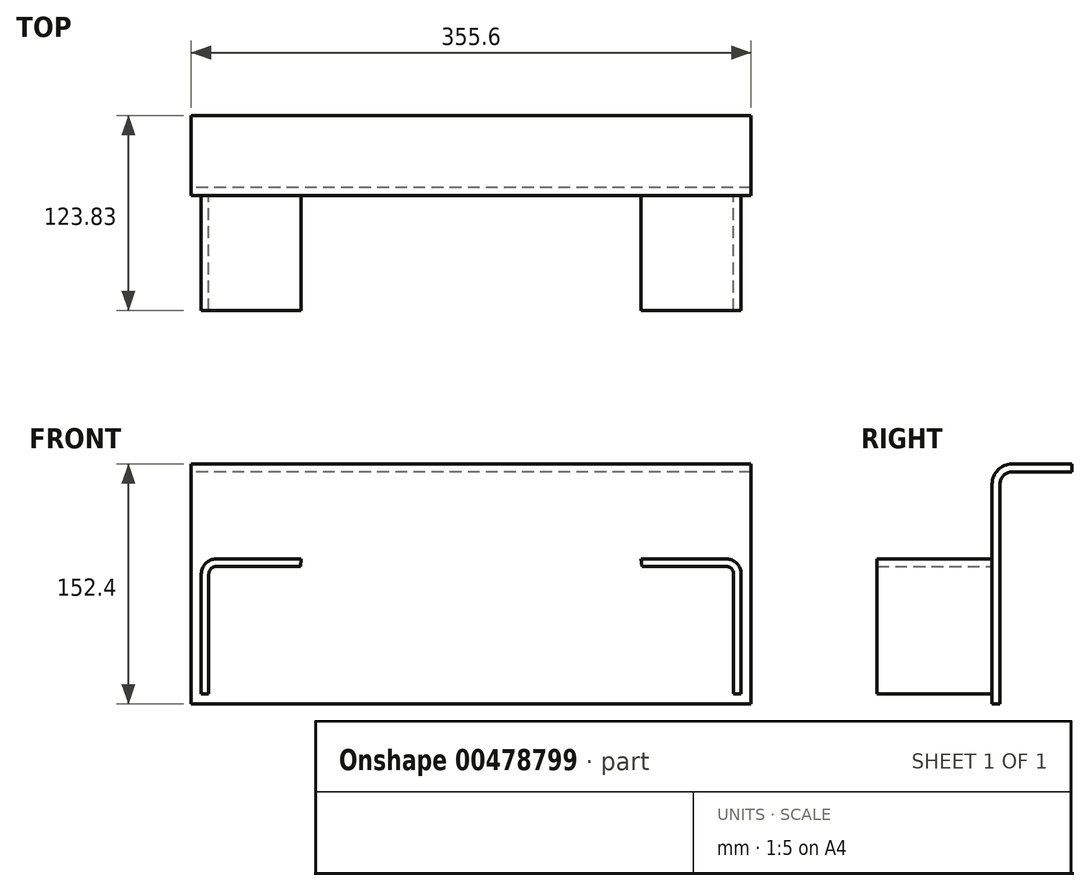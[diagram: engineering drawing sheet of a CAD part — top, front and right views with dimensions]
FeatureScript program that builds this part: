
annotation { "Feature Type Name" : "Feature", "Feature Type Description" : "" }
export const myFeature = defineFeature(function(context is Context, id is Id, definition is map)
    precondition{}
    {
        {
            var Q0;
            Q0=qCreatedBy(makeId("Right.planeOp"),FACE);
            var sketch = newSketch(context, id + "F0", { "sketchPlane" : qUnion([Q0])});
            skLineSegment(sketch, "E0", {"start": v(0, -152.4) * mm, "end": v(0, -12.7) * mm});
            skLineSegment(sketch, "E1", {"start": v(12.7, 0) * mm, "end": v(50.8, 0) * mm});
            skPoint(sketch, "E2.visualSharp", {"position": v(0, 0) * mm});
            skArc(sketch, "E2.filletArc", {"start": v(12.7, 0) * mm, "mid": v(3.72, -3.72) * mm, "end": v(0, -12.7) * mm});
            skLineSegment(sketch, "E3.0", {"start": v(5.03, -152.4) * mm, "end": v(5.03, -12.7) * mm});
            skArc(sketch, "E3.1", {"start": v(12.7, -5.03) * mm, "mid": v(7.27, -7.27) * mm, "end": v(5.03, -12.7) * mm});
            skLineSegment(sketch, "E3.2", {"start": v(12.7, -5.03) * mm, "end": v(50.8, -5.03) * mm});
            skLineSegment(sketch, "E4", {"start": v(50.8, 0) * mm, "end": v(50.8, -5.03) * mm});
            skLineSegment(sketch, "E5", {"start": v(5.03, -152.4) * mm, "end": v(0, -152.4) * mm});
            skSolve(sketch);
        }
        {
            var Q0;
            Q0=makeQuery(id+"F0.imprint","IMPRINT",FACE,{"disambiguationData":[TD([[makeQuery(id+"F0.imprint","IMPRINT",EDGE,{"derivedFrom":sQuery(id+"F0.wireOp",EDGE,"E0")}),-1.0]])]});
            extrude(context, id + "F1", {"entities" : qUnion([Q0]), "endBound" : BoundingType.SYMMETRIC, "depth" : 355.6 * mm});
        }
        {
            var Q0;
            Q0=makeQuery(id+"F1.opExtrude","SWEPT_FACE",FACE,{"disambiguationData":[OSD([sQuery(id+"F0.wireOp",EDGE,"E0")])]});
            var sketch = newSketch(context, id + "F2", { "sketchPlane" : qUnion([Q0])});
            skLineSegment(sketch, "E6", {"start": v(-107.95, -60.33) * mm, "end": v(-161.92, -60.33) * mm});
            skLineSegment(sketch, "E7", {"start": v(-171.45, -69.85) * mm, "end": v(-171.45, -155.58) * mm});
            skPoint(sketch, "E8.visualSharp", {"position": v(-171.45, -60.33) * mm});
            skArc(sketch, "E8.filletArc", {"start": v(-161.92, -60.33) * mm, "mid": v(-168.66, -63.11) * mm, "end": v(-171.45, -69.85) * mm});
            skLineSegment(sketch, "E9.0", {"start": v(-166.69, -69.85) * mm, "end": v(-166.69, -155.92) * mm});
            skArc(sketch, "E9.1", {"start": v(-161.92, -65.09) * mm, "mid": v(-165.3, -66.48) * mm, "end": v(-166.69, -69.85) * mm});
            skLineSegment(sketch, "E9.2", {"start": v(-108.3, -65.09) * mm, "end": v(-161.92, -65.09) * mm});
            skLineSegment(sketch, "E10.0", {"start": v(-171.45, -19.05) * mm, "end": v(-171.45, -146.05) * mm});
            skLineSegment(sketch, "E10.1", {"start": v(171.45, -19.05) * mm, "end": v(-171.45, -19.05) * mm});
            skLineSegment(sketch, "E10.2", {"start": v(171.45, -146.05) * mm, "end": v(171.45, -19.05) * mm});
            skLineSegment(sketch, "E10.3", {"start": v(-171.45, -146.05) * mm, "end": v(171.45, -146.05) * mm});
            skLineSegment(sketch, "E11", {"start": v(-107.95, -60.33) * mm, "end": v(-108.3, -65.09) * mm});
            skLineSegment(sketch, "E12", {"start": v(-166.69, -155.92) * mm, "end": v(-171.45, -155.57) * mm});
            skSolve(sketch);
        }
        {
            var Q0;
            Q0=makeQuery(id+"F2.imprint","IMPRINT",FACE,{"disambiguationData":[TD([[makeQuery(id+"F2.imprint","IMPRINT",EDGE,{"derivedFrom":sQuery(id+"F2.wireOp",EDGE,"E6")}),1.0]])]});
            extrude(context, id + "F3", {"entities" : qUnion([Q0]), "depth" : 73.02 * mm, "offsetDistance" : 25.4 * mm});
        }
        {
            var Q0;
            Q0=makeQuery(id+"F3.opExtrude","SWEPT_BODY",BODY,{"disambiguationData":[OSD([sQuery(id+"F2.wireOp",EDGE,"E6"),sQuery(id+"F2.wireOp",EDGE,"E8.filletArc"),sQuery(id+"F2.wireOp",EDGE,"E9.0"),sQuery(id+"F2.wireOp",EDGE,"E9.1"),sQuery(id+"F2.wireOp",EDGE,"E9.2"),sQuery(id+"F2.wireOp",EDGE,"E10.0"),sQuery(id+"F2.wireOp",EDGE,"E10.3"),sQuery(id+"F2.wireOp",EDGE,"E11")])]});
            var Q1;
            Q1=qCreatedBy(makeId("Right.planeOp"),FACE);
            mirror(context, id + "F4", {"entities" : qUnion([Q0]), "mirrorPlane" : qUnion([Q1])});
        }
    });
